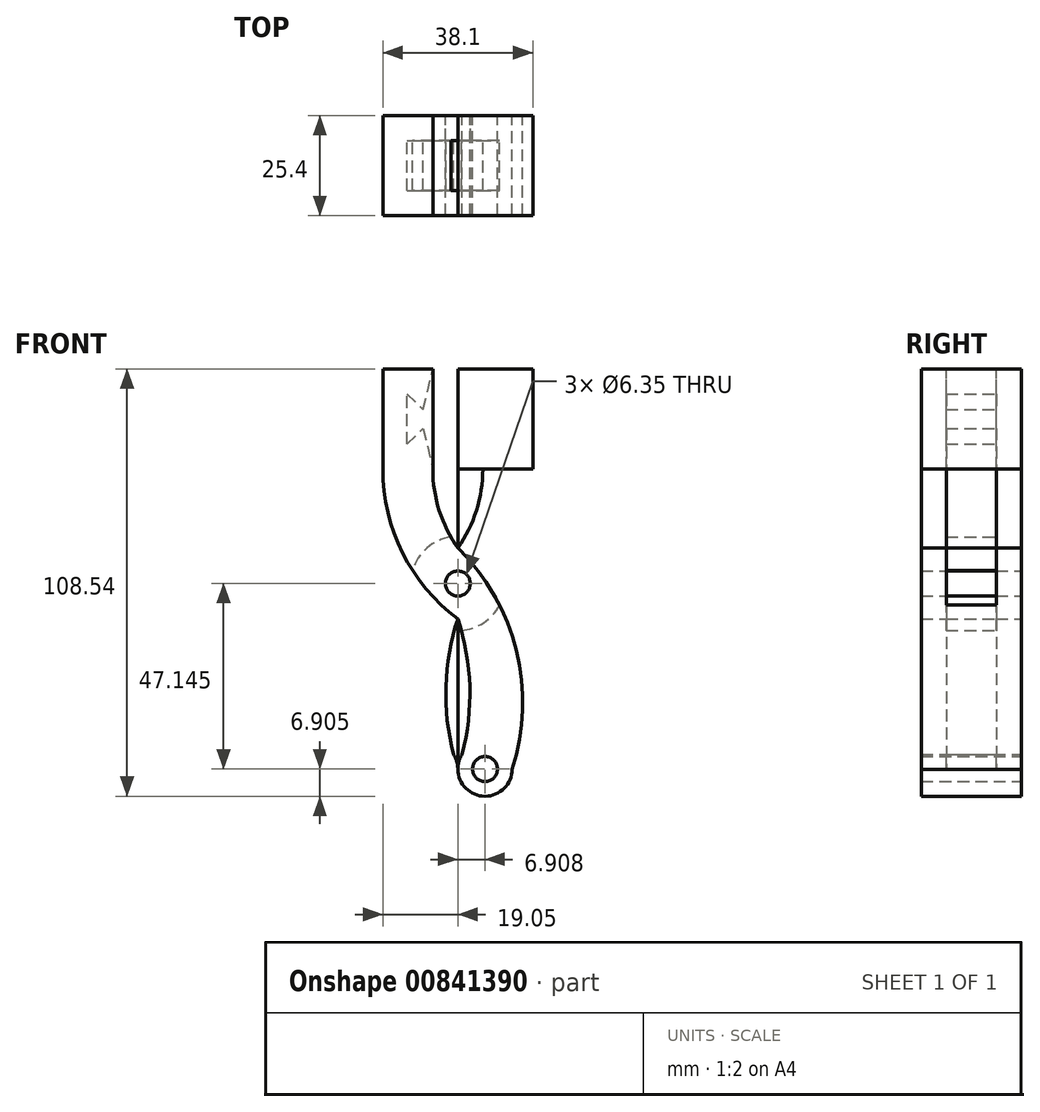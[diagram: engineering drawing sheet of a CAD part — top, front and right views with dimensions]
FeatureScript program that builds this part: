
annotation { "Feature Type Name" : "Feature", "Feature Type Description" : "" }
export const myFeature = defineFeature(function(context is Context, id is Id, definition is map)
    precondition{}
    {
        {
            var Q0;
            Q0=qCreatedBy(makeId("Front.planeOp"),FACE);
            var sketch = newSketch(context, id + "F0", { "sketchPlane" : qUnion([Q0])});
            skLineSegment(sketch, "E0.bottom", {"start": v(0, 0) * mm, "end": v(19.05, 0) * mm});
            skLineSegment(sketch, "E0.top", {"start": v(0, -25.4) * mm, "end": v(19.05, -25.4) * mm});
            skLineSegment(sketch, "E0.left", {"start": v(0, 0) * mm, "end": v(0, -25.4) * mm});
            skLineSegment(sketch, "E0.right", {"start": v(19.05, 0) * mm, "end": v(19.05, -25.4) * mm});
            skLineSegment(sketch, "E1.MirrorCS", {"start": v(0, 0) * mm, "end": v(-19.05, 0) * mm});
            skLineSegment(sketch, "E2.MirrorCS", {"start": v(-19.05, 0) * mm, "end": v(-19.05, -25.4) * mm});
            skLineSegment(sketch, "E3.MirrorCS", {"start": v(0, -25.4) * mm, "end": v(-6.35, -25.4) * mm});
            skLineSegment(sketch, "E4", {"start": v(0, -25.4) * mm, "end": v(0, -45.48) * mm});
            skArc(sketch, "E5", {"start": v(-19.05, -25.4) * mm, "mid": v(-14.02, -46.7) * mm, "end": v(0, -63.5) * mm});
            skArc(sketch, "E6.0", {"start": v(-6.35, -25.4) * mm, "mid": v(-4.72, -35.93) * mm, "end": v(0, -45.48) * mm});
            skArc(sketch, "E7", {"start": v(13.82, -101.67) * mm, "mid": v(14.87, -71.62) * mm, "end": v(0, -45.48) * mm});
            skArc(sketch, "E8", {"start": v(1.09, -97.91) * mm, "mid": v(3.03, -80.63) * mm, "end": v(0, -63.5) * mm});
            skLineSegment(sketch, "E9.trimOffspring", {"start": v(0, -63.5) * mm, "end": v(0, -101.6) * mm});
            skArc(sketch, "E10", {"start": v(1.09, -97.91) * mm, "mid": v(4.95, -108.26) * mm, "end": v(13.82, -101.67) * mm});
            skLineSegment(sketch, "E11", {"start": v(0, -45.48) * mm, "end": v(0, -63.5) * mm});
            skCircle(sketch, "E12", {"center": v(0, -54.5) * mm, "radius": 3.18 * mm});
            skPoint(sketch, "E13.orphan", {"position": v(-19.05, -25.4) * mm});
            skLineSegment(sketch, "E14", {"start": v(-19.05, -25.4) * mm, "end": v(-6.35, -25.4) * mm});
            skArc(sketch, "E15.MirrorCS", {"start": v(6.35, -25.4) * mm, "mid": v(4.72, -35.93) * mm, "end": v(0, -45.48) * mm});
            skArc(sketch, "E16.MirrorCS", {"start": v(19.05, -25.4) * mm, "mid": v(14.02, -46.7) * mm, "end": v(0, -63.5) * mm});
            skArc(sketch, "E17.MirrorCS", {"start": v(-13.82, -101.67) * mm, "mid": v(-14.87, -71.62) * mm, "end": v(0, -45.48) * mm});
            skArc(sketch, "E18.MirrorCS", {"start": v(-1.09, -97.91) * mm, "mid": v(-3.03, -80.63) * mm, "end": v(0, -63.5) * mm});
            skArc(sketch, "E19.MirrorCS", {"start": v(-1.09, -97.91) * mm, "mid": v(-4.95, -108.26) * mm, "end": v(-13.82, -101.67) * mm});
            skLineSegment(sketch, "E20", {"start": v(-6.35, -25.4) * mm, "end": v(-6.35, 0) * mm});
            skLineSegment(sketch, "E21", {"start": v(-12.94, -12.7) * mm, "end": v(-12.94, -6.35) * mm});
            skLineSegment(sketch, "E22", {"start": v(-12.94, -6.35) * mm, "end": v(-8.83, -10.31) * mm});
            skLineSegment(sketch, "E23.MirrorCS", {"start": v(-12.94, -19.05) * mm, "end": v(-8.83, -15.09) * mm});
            skLineSegment(sketch, "E24.MirrorCS", {"start": v(-12.94, -12.7) * mm, "end": v(-12.94, -19.05) * mm});
            skLineSegment(sketch, "E25.MirrorCS", {"start": v(12.94, -6.35) * mm, "end": v(8.83, -10.31) * mm});
            skLineSegment(sketch, "E26.MirrorCS", {"start": v(12.94, -12.7) * mm, "end": v(12.94, -6.35) * mm});
            skLineSegment(sketch, "E27.MirrorCS", {"start": v(12.94, -12.7) * mm, "end": v(12.94, -19.05) * mm});
            skLineSegment(sketch, "E28.MirrorCS", {"start": v(12.94, -19.05) * mm, "end": v(8.83, -15.09) * mm});
            skLineSegment(sketch, "E29.MirrorCS", {"start": v(6.35, -25.4) * mm, "end": v(6.35, 0) * mm});
            skLineSegment(sketch, "E30", {"start": v(-8.83, -10.31) * mm, "end": v(-6.35, 0) * mm});
            skLineSegment(sketch, "E31", {"start": v(-8.83, -15.09) * mm, "end": v(-6.35, -25.4) * mm});
            skPoint(sketch, "E32.MirrorCS.end.orphan", {"position": v(-6.35, -15.09) * mm});
            skPoint(sketch, "E32.MirrorCS.start.orphan", {"position": v(-8.83, -15.09) * mm});
            skPoint(sketch, "E33.end.orphan", {"position": v(-6.35, -10.31) * mm});
            skLineSegment(sketch, "E34", {"start": v(8.83, -10.31) * mm, "end": v(6.35, 0) * mm});
            skLineSegment(sketch, "E35", {"start": v(8.83, -15.09) * mm, "end": v(6.35, -25.4) * mm});
            skPoint(sketch, "E36.MirrorCS.end.orphan", {"position": v(6.35, -10.31) * mm});
            skPoint(sketch, "E36.MirrorCS.start.orphan", {"position": v(8.83, -10.31) * mm});
            skPoint(sketch, "E37.MirrorCS.end.orphan", {"position": v(6.35, -15.09) * mm});
            skPoint(sketch, "E37.MirrorCS.start.orphan", {"position": v(8.83, -15.09) * mm});
            skPoint(sketch, "E38.start.orphan", {"position": v(-6.35, -12.7) * mm});
            skCircle(sketch, "E39", {"center": v(-6.9, -101.64) * mm, "radius": 3.18 * mm});
            skCircle(sketch, "E40", {"center": v(6.9, -101.64) * mm, "radius": 3.18 * mm});
            skArc(sketch, "E41.trimOffspring", {"start": v(-1.77, -42.69) * mm, "mid": v(-7.86, -45.52) * mm, "end": v(-11.47, -51.18) * mm});
            skArc(sketch, "E42.trimOffspring", {"start": v(0.88, -66.4) * mm, "mid": v(6.56, -64.46) * mm, "end": v(10.58, -60) * mm});
            skSolve(sketch);
        }
        {
            var Q0;
            {var subQ0=sQuery(id+"F0.wireOp",EDGE,"E2.MirrorCS");Q0=makeQuery(id+"F0.imprint","IMPRINT",FACE,{"disambiguationData":[TD([[makeQuery(id+"F0.imprint","IMPRINT",EDGE,{"derivedFrom":subQ0}),1.0]])]});}
            var Q1;
            {var subQ0=sQuery(id+"F0.wireOp",EDGE,"E0.right");Q1=makeQuery(id+"F0.imprint","IMPRINT",FACE,{"disambiguationData":[TD([[makeQuery(id+"F0.imprint","IMPRINT",EDGE,{"derivedFrom":subQ0}),-1.0]])]});}
            var Q2;
            Q2=makeQuery(id+"F0.imprint","IMPRINT",FACE,{"disambiguationData":[TD([[makeQuery(id+"F0.imprint","IMPRINT",EDGE,{"derivedFrom":sQuery(id+"F0.wireOp",EDGE,"E26.MirrorCS")}),1.0]])]});
            var Q3;
            Q3=makeQuery(id+"F0.imprint","IMPRINT",FACE,{"disambiguationData":[TD([[makeQuery(id+"F0.imprint","IMPRINT",EDGE,{"derivedFrom":sQuery(id+"F0.wireOp",EDGE,"E20")}),1.0]])]});
            extrude(context, id + "F1", {"entities" : qUnion([Q0, Q1, Q2, Q3]), "oppositeDirection" : true, "depth" : 12.7 * mm, "offsetDistance" : 25.4 * mm, "hasSecondDirection" : true, "secondDirectionOppositeDirection" : false, "secondDirectionDepth" : 12.7 * mm});
        }
        {
            var Q0;
            Q0=makeQuery(id+"F0.imprint","IMPRINT",FACE,{"disambiguationData":[TD([[makeQuery(id+"F0.imprint","IMPRINT",EDGE,{"derivedFrom":sQuery(id+"F0.wireOp",EDGE,"E26.MirrorCS")}),1.0]])]});
            var Q1;
            Q1=makeQuery(id+"F0.imprint","IMPRINT",FACE,{"disambiguationData":[TD([[makeQuery(id+"F0.imprint","IMPRINT",EDGE,{"derivedFrom":sQuery(id+"F0.wireOp",EDGE,"E20")}),1.0]])]});
            extrude(context, id + "F2", {"entities" : qUnion([Q0, Q1]), "operationType" : NewBodyOperationType.REMOVE, "depth" : 6.35 * mm, "offsetDistance" : 25.4 * mm, "hasSecondDirection" : true, "secondDirectionOppositeDirection" : true, "secondDirectionDepth" : 6.35 * mm});
        }
        {
            var Q0;
            Q0=makeQuery(id+"F0.imprint","IMPRINT",FACE,{"disambiguationData":[TD([[makeQuery(id+"F0.imprint","IMPRINT",EDGE,{"derivedFrom":sQuery(id+"F0.wireOp",EDGE,"E26.MirrorCS")}),1.0]])]});
            extrude(context, id + "F3", {"entities" : qUnion([Q0]), "depth" : 6.35 * mm, "offsetDistance" : 25.4 * mm, "hasSecondDirection" : true, "secondDirectionOppositeDirection" : true, "secondDirectionDepth" : 6.35 * mm});
        }
        {
            var Q0;
            {var subQ0=sQuery(id+"F0.wireOp",EDGE,"E0.left");Q0=makeQuery(id+"F0.imprint","IMPRINT",FACE,{"disambiguationData":[TD([[makeQuery(id+"F0.imprint","IMPRINT",EDGE,{"derivedFrom":subQ0}),1.0]])]});}
            extrude(context, id + "F4", {"entities" : qUnion([Q0]), "operationType" : NewBodyOperationType.ADD, "depth" : 12.7 * mm, "offsetDistance" : 25.4 * mm, "hasSecondDirection" : true, "secondDirectionOppositeDirection" : true, "secondDirectionDepth" : 12.7 * mm});
        }
        {
            var Q0;
            {var subQ3=sQuery(id+"F0.wireOp",EDGE,"E15.MirrorCS");Q0=makeQuery(id+"F0.imprint","IMPRINT",FACE,{"disambiguationData":[TD([[makeQuery(id+"F0.imprint","IMPRINT",EDGE,{"derivedFrom":subQ3}),1.0]])]});}
            var Q1;
            {var subQ0=sQuery(id+"F0.wireOp",EDGE,"E12");var subQ1=sQuery(id+"F0.wireOp",EDGE,"E11");var subQ2=makeQuery(id+"F0.imprint","INTERSECT",VERTEX,{"disambiguationData":[OD(0.0)],"derivedFrom":[subQ1,subQ0]});Q1=makeQuery(id+"F0.imprint","IMPRINT",FACE,{"disambiguationData":[TD([[makeQuery(id+"F0.imprint","IMPRINT",EDGE,{"disambiguationData":[TD([[subQ2,1.0]])],"derivedFrom":subQ0}),-1.0]])]});}
            var Q2;
            {var subQ0=sQuery(id+"F0.wireOp",EDGE,"E12");var subQ1=sQuery(id+"F0.wireOp",EDGE,"E11");var subQ2=makeQuery(id+"F0.imprint","INTERSECT",VERTEX,{"disambiguationData":[OD(0.0)],"derivedFrom":[subQ1,subQ0]});Q2=makeQuery(id+"F0.imprint","IMPRINT",FACE,{"disambiguationData":[TD([[makeQuery(id+"F0.imprint","IMPRINT",EDGE,{"disambiguationData":[TD([[subQ2,-1.0]])],"derivedFrom":subQ0}),-1.0]])]});}
            var Q3;
            {var subQ0=sQuery(id+"F0.wireOp",EDGE,"E18.MirrorCS");Q3=makeQuery(id+"F0.imprint","IMPRINT",FACE,{"disambiguationData":[TD([[makeQuery(id+"F0.imprint","IMPRINT",EDGE,{"derivedFrom":subQ0}),1.0]])]});}
            extrude(context, id + "F5", {"entities" : qUnion([Q0, Q1, Q2, Q3]), "operationType" : NewBodyOperationType.ADD, "depth" : 6.35 * mm, "offsetDistance" : 25.4 * mm, "hasSecondDirection" : true, "secondDirectionOppositeDirection" : true, "secondDirectionDepth" : 6.35 * mm});
        }
        {
            var Q0;
            {var subQ4=sQuery(id+"F0.wireOp",EDGE,"E6.0");Q0=makeQuery(id+"F0.imprint","IMPRINT",FACE,{"disambiguationData":[TD([[makeQuery(id+"F0.imprint","IMPRINT",EDGE,{"derivedFrom":subQ4}),-1.0]])]});}
            var Q1;
            {var subQ0=sQuery(id+"F0.wireOp",EDGE,"E12");var subQ1=sQuery(id+"F0.wireOp",EDGE,"E11");var subQ2=makeQuery(id+"F0.imprint","INTERSECT",VERTEX,{"disambiguationData":[OD(0.0)],"derivedFrom":[subQ1,subQ0]});Q1=makeQuery(id+"F0.imprint","IMPRINT",FACE,{"disambiguationData":[TD([[makeQuery(id+"F0.imprint","IMPRINT",EDGE,{"disambiguationData":[TD([[subQ2,-1.0]])],"derivedFrom":subQ0}),-1.0]])]});}
            var Q2;
            {var subQ0=sQuery(id+"F0.wireOp",EDGE,"E12");var subQ1=sQuery(id+"F0.wireOp",EDGE,"E11");var subQ2=makeQuery(id+"F0.imprint","INTERSECT",VERTEX,{"disambiguationData":[OD(0.0)],"derivedFrom":[subQ1,subQ0]});Q2=makeQuery(id+"F0.imprint","IMPRINT",FACE,{"disambiguationData":[TD([[makeQuery(id+"F0.imprint","IMPRINT",EDGE,{"disambiguationData":[TD([[subQ2,1.0]])],"derivedFrom":subQ0}),-1.0]])]});}
            var Q3;
            {var subQ1=sQuery(id+"F0.wireOp",EDGE,"E8");Q3=makeQuery(id+"F0.imprint","IMPRINT",FACE,{"disambiguationData":[TD([[makeQuery(id+"F0.imprint","IMPRINT",EDGE,{"derivedFrom":subQ1}),-1.0]])]});}
            var Q4;
            Q4=makeQuery(id+"F0.imprint","IMPRINT",FACE,{"disambiguationData":[TD([[makeQuery(id+"F0.imprint","IMPRINT",EDGE,{"derivedFrom":sQuery(id+"F0.wireOp",EDGE,"E40")}),-1.0]])]});
            extrude(context, id + "F6", {"entities" : qUnion([Q0, Q1, Q2, Q3, Q4]), "operationType" : NewBodyOperationType.ADD, "depth" : 12.7 * mm, "offsetDistance" : 25.4 * mm, "hasSecondDirection" : true, "secondDirectionOppositeDirection" : true, "secondDirectionDepth" : 12.7 * mm});
        }
        {
            var Q0;
            {var subQ0=sQuery(id+"F0.wireOp",EDGE,"E41.trimOffspring");Q0=makeQuery(id+"F0.imprint","IMPRINT",FACE,{"disambiguationData":[TD([[makeQuery(id+"F0.imprint","IMPRINT",EDGE,{"derivedFrom":subQ0}),1.0]])]});}
            var Q1;
            {var subQ0=sQuery(id+"F0.wireOp",EDGE,"E12");var subQ1=sQuery(id+"F0.wireOp",EDGE,"E11");var subQ2=makeQuery(id+"F0.imprint","INTERSECT",VERTEX,{"disambiguationData":[OD(0.0)],"derivedFrom":[subQ1,subQ0]});Q1=makeQuery(id+"F0.imprint","IMPRINT",FACE,{"disambiguationData":[TD([[makeQuery(id+"F0.imprint","IMPRINT",EDGE,{"disambiguationData":[TD([[subQ2,-1.0]])],"derivedFrom":subQ0}),-1.0]])]});}
            var Q2;
            {var subQ1=sQuery(id+"F0.wireOp",EDGE,"E11");var subQ3=sQuery(id+"F0.wireOp",EDGE,"E12");var subQ7=makeQuery(id+"F0.imprint","INTERSECT",VERTEX,{"disambiguationData":[OD(0.0)],"derivedFrom":[subQ1,subQ3]});Q2=makeQuery(id+"F0.imprint","IMPRINT",FACE,{"disambiguationData":[TD([[makeQuery(id+"F0.imprint","IMPRINT",EDGE,{"disambiguationData":[TD([[subQ7,1.0]])],"derivedFrom":subQ3}),-1.0]])]});}
            var Q3;
            {var subQ0=sQuery(id+"F0.wireOp",EDGE,"E42.trimOffspring");Q3=makeQuery(id+"F0.imprint","IMPRINT",FACE,{"disambiguationData":[TD([[makeQuery(id+"F0.imprint","IMPRINT",EDGE,{"derivedFrom":subQ0}),1.0]])]});}
            extrude(context, id + "F7", {"entities" : qUnion([Q0, Q1, Q2, Q3]), "operationType" : NewBodyOperationType.REMOVE, "depth" : 6.35 * mm, "offsetDistance" : 25.4 * mm, "hasSecondDirection" : true, "secondDirectionOppositeDirection" : true, "secondDirectionDepth" : 6.35 * mm});
        }
        {
            var Q0;
            {var subQ0=sQuery(id+"F0.wireOp",EDGE,"E12");var subQ1=sQuery(id+"F0.wireOp",EDGE,"E11");var subQ2=makeQuery(id+"F0.imprint","INTERSECT",VERTEX,{"disambiguationData":[OD(0.0)],"derivedFrom":[subQ1,subQ0]});Q0=makeQuery(id+"F0.imprint","IMPRINT",FACE,{"disambiguationData":[TD([[makeQuery(id+"F0.imprint","IMPRINT",EDGE,{"disambiguationData":[TD([[subQ2,-1.0]])],"derivedFrom":subQ1}),-1.0]])]});}
            var Q1;
            {var subQ0=sQuery(id+"F0.wireOp",EDGE,"E12");var subQ1=sQuery(id+"F0.wireOp",EDGE,"E11");var subQ2=makeQuery(id+"F0.imprint","INTERSECT",VERTEX,{"disambiguationData":[OD(0.0)],"derivedFrom":[subQ1,subQ0]});Q1=makeQuery(id+"F0.imprint","IMPRINT",FACE,{"disambiguationData":[TD([[makeQuery(id+"F0.imprint","IMPRINT",EDGE,{"disambiguationData":[TD([[subQ2,-1.0]])],"derivedFrom":subQ1}),1.0]])]});}
            extrude(context, id + "F8", {"entities" : qUnion([Q0, Q1]), "depth" : 12.7 * mm, "offsetDistance" : 25.4 * mm, "hasSecondDirection" : true, "secondDirectionOppositeDirection" : true, "secondDirectionDepth" : 12.7 * mm});
        }
    });
